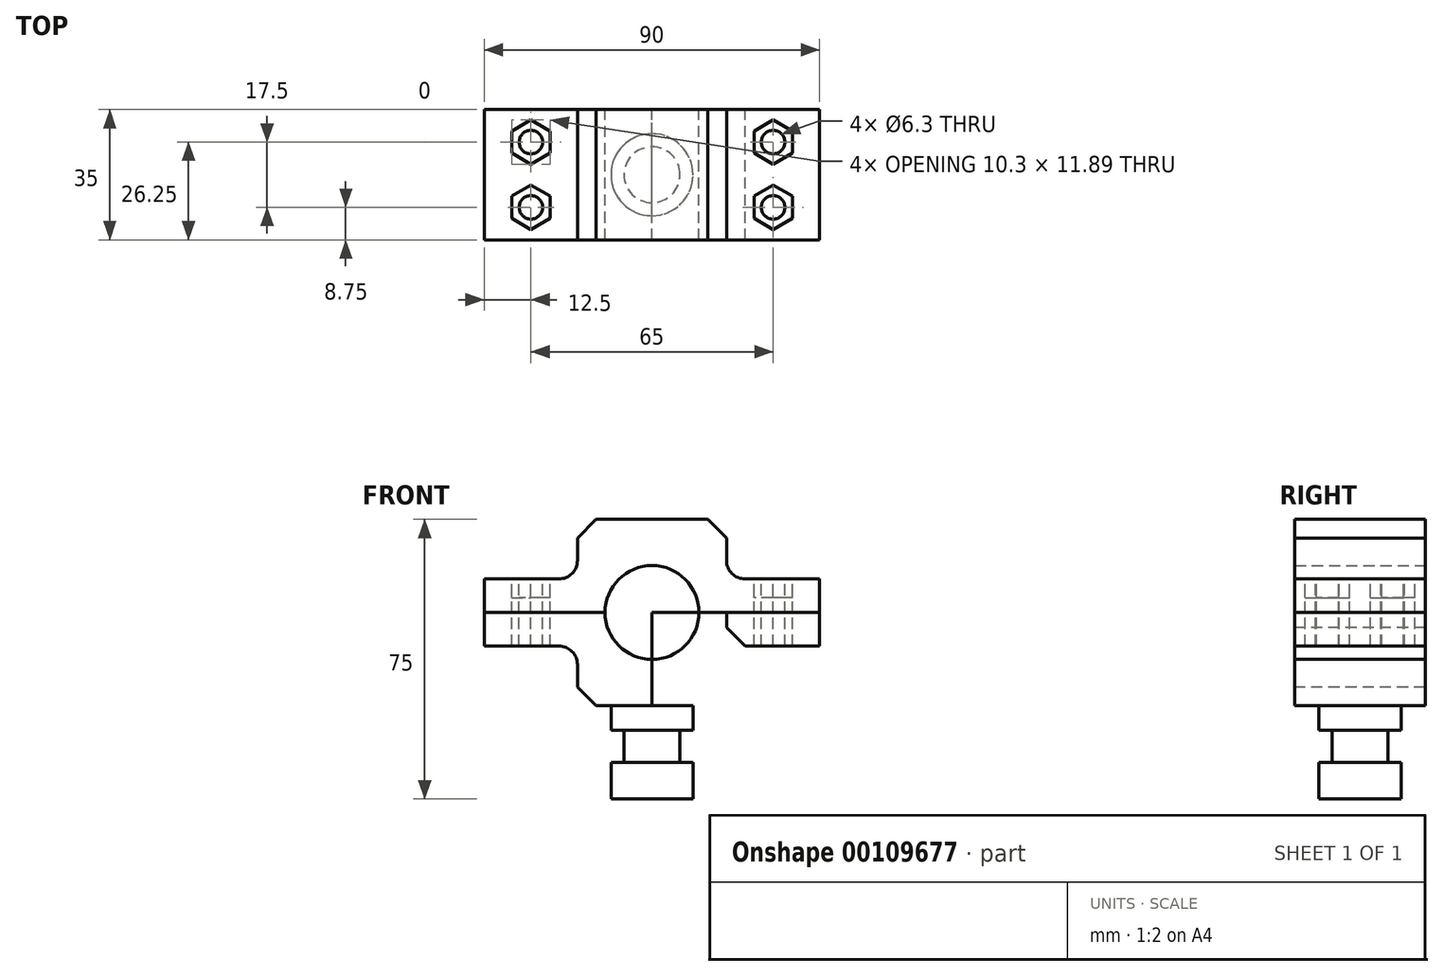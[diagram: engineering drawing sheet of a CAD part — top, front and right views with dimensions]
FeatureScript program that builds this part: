
annotation { "Feature Type Name" : "Feature", "Feature Type Description" : "" }
export const myFeature = defineFeature(function(context is Context, id is Id, definition is map)
    precondition{}
    {
        {
            var Q0;
            Q0=qCreatedBy(makeId("Front.planeOp"),FACE);
            var sketch = newSketch(context, id + "F8", { "sketchPlane" : qUnion([Q0])});
            skArc(sketch, "E0", {"start": v(12.6, 0) * mm, "mid": v(8.9, 8.9) * mm, "end": v(0, 12.6) * mm});
            skLineSegment(sketch, "E1", {"start": v(0, 25) * mm, "end": v(20, 25) * mm});
            skLineSegment(sketch, "E2", {"start": v(20, 25) * mm, "end": v(20, 0) * mm});
            skLineSegment(sketch, "E3", {"start": v(20, 0) * mm, "end": v(45, 0) * mm});
            skLineSegment(sketch, "E4", {"start": v(45, 0) * mm, "end": v(45, 9) * mm});
            skLineSegment(sketch, "E5", {"start": v(45, 9) * mm, "end": v(45, 9) * mm});
            skLineSegment(sketch, "E6", {"start": v(20, 9) * mm, "end": v(45, 9) * mm});
            skLineSegment(sketch, "E7", {"start": v(0, 28.76) * mm, "end": v(0, -27.9) * mm});
            skLineSegment(sketch, "E8", {"start": v(-45, 0) * mm, "end": v(28.7, 0) * mm});
            skLineSegment(sketch, "E9.MirrorCS", {"start": v(0, 25) * mm, "end": v(-20, 25) * mm});
            skArc(sketch, "E10.MirrorCS", {"start": v(-12.6, 0) * mm, "mid": v(-8.9, 8.9) * mm, "end": v(0, 12.6) * mm});
            skLineSegment(sketch, "E11.MirrorCS", {"start": v(-20, 25) * mm, "end": v(-20, 0) * mm});
            skLineSegment(sketch, "E12.MirrorCS", {"start": v(-20, 9) * mm, "end": v(-45, 9) * mm});
            skLineSegment(sketch, "E13.MirrorCS", {"start": v(-45, 0) * mm, "end": v(-45, 9) * mm});
            skArc(sketch, "E14.MirrorCS", {"start": v(12.6, 0) * mm, "mid": v(8.9, -8.9) * mm, "end": v(0, -12.6) * mm});
            skArc(sketch, "E15.MirrorCS", {"start": v(-12.6, 0) * mm, "mid": v(-8.9, -8.9) * mm, "end": v(0, -12.6) * mm});
            skLineSegment(sketch, "E16.MirrorCS", {"start": v(0, -25) * mm, "end": v(20, -25) * mm});
            skLineSegment(sketch, "E17.MirrorCS", {"start": v(20, -25) * mm, "end": v(20, 0) * mm});
            skLineSegment(sketch, "E18.MirrorCS", {"start": v(20, -9) * mm, "end": v(45, -9) * mm});
            skLineSegment(sketch, "E19.MirrorCS", {"start": v(45, 0) * mm, "end": v(45, -9) * mm});
            skLineSegment(sketch, "E20.MirrorCS", {"start": v(0, -25) * mm, "end": v(-20, -25) * mm});
            skLineSegment(sketch, "E21.MirrorCS", {"start": v(-20, -25) * mm, "end": v(-20, 0) * mm});
            skLineSegment(sketch, "E22.MirrorCS", {"start": v(-20, -9) * mm, "end": v(-45, -9) * mm});
            skLineSegment(sketch, "E23.MirrorCS", {"start": v(-45, 0) * mm, "end": v(-45, -9) * mm});
            skSolve(sketch);
        }
        {
            var Q0;
            {var subQ2=sQuery(id+"F8.wireOp",EDGE,"E9.MirrorCS");Q0=makeQuery(id+"F8.imprint","IMPRINT",FACE,{"disambiguationData":[TD([[makeQuery(id+"F8.imprint","IMPRINT",EDGE,{"derivedFrom":subQ2}),1.0]])]});}
            var Q1;
            {var subQ4=sQuery(id+"F8.wireOp",EDGE,"E4");Q1=makeQuery(id+"F8.imprint","IMPRINT",FACE,{"disambiguationData":[TD([[makeQuery(id+"F8.imprint","IMPRINT",EDGE,{"derivedFrom":subQ4}),1.0]])]});}
            var Q2;
            {var subQ4=sQuery(id+"F8.wireOp",EDGE,"E12.MirrorCS");Q2=makeQuery(id+"F8.imprint","IMPRINT",FACE,{"disambiguationData":[TD([[makeQuery(id+"F8.imprint","IMPRINT",EDGE,{"derivedFrom":subQ4}),1.0]])]});}
            var Q3;
            {var subQ5=sQuery(id+"F8.wireOp",EDGE,"E0");Q3=makeQuery(id+"F8.imprint","IMPRINT",FACE,{"disambiguationData":[TD([[makeQuery(id+"F8.imprint","IMPRINT",EDGE,{"derivedFrom":subQ5}),-1.0]])]});}
            extrude(context, id + "F9", {"entities" : qUnion([Q0, Q1, Q2, Q3]), "depth" : 35 * mm});
        }
        {
            var Q0;
            Q0=makeQuery(id+"F9.opExtrude","SWEPT_FACE",FACE,{"disambiguationData":[OSD([sQuery(id+"F8.wireOp",EDGE,"E6")])]});
            var sketch = newSketch(context, id + "F0", { "sketchPlane" : qUnion([Q0])});
            skLineSegment(sketch, "E24", {"start": v(20, -17.5) * mm, "end": v(45, -17.5) * mm, "construction": true});
            skLineSegment(sketch, "E25", {"start": v(20, -8.75) * mm, "end": v(45, -8.75) * mm, "construction": true});
            skLineSegment(sketch, "E26", {"start": v(45, -17.5) * mm, "end": v(45, -8.75) * mm});
            skCircle(sketch, "E27.cCircle", {"center": v(32.5, -8.75) * mm, "radius": 5.95 * mm, "construction": true});
            skPoint(sketch, "E27.cCircle.perimeterSnap0", {"position": v(32.5, -8.75) * mm});
            skLineSegment(sketch, "E27.0", {"start": v(32.5, -14.7) * mm, "end": v(27.35, -11.72) * mm});
            skPoint(sketch, "E27.0.startSnap0", {"position": v(32.5, -8.75) * mm});
            skLineSegment(sketch, "E27.1", {"start": v(27.35, -11.72) * mm, "end": v(27.35, -5.78) * mm});
            skLineSegment(sketch, "E27.2", {"start": v(27.35, -5.78) * mm, "end": v(32.5, -2.8) * mm});
            skLineSegment(sketch, "E27.3", {"start": v(32.5, -2.8) * mm, "end": v(37.65, -5.78) * mm});
            skLineSegment(sketch, "E27.4", {"start": v(37.65, -5.78) * mm, "end": v(37.65, -11.72) * mm});
            skLineSegment(sketch, "E27.5", {"start": v(37.65, -11.72) * mm, "end": v(32.5, -14.7) * mm});
            skLineSegment(sketch, "E28.MirrorCS", {"start": v(32.5, -32.2) * mm, "end": v(37.65, -29.22) * mm});
            skLineSegment(sketch, "E29.MirrorCS", {"start": v(20, -26.25) * mm, "end": v(45, -26.25) * mm, "construction": true});
            skCircle(sketch, "E30.MirrorC", {"center": v(32.5, -26.25) * mm, "radius": 5.95 * mm, "construction": true});
            skLineSegment(sketch, "E31.MirrorCS", {"start": v(37.65, -29.22) * mm, "end": v(37.65, -23.28) * mm});
            skLineSegment(sketch, "E32.MirrorCS", {"start": v(27.35, -29.22) * mm, "end": v(32.5, -32.2) * mm});
            skLineSegment(sketch, "E33.MirrorCS", {"start": v(27.35, -23.28) * mm, "end": v(27.35, -29.22) * mm});
            skLineSegment(sketch, "E34.MirrorCS", {"start": v(37.65, -23.28) * mm, "end": v(32.5, -20.3) * mm});
            skLineSegment(sketch, "E35.MirrorCS", {"start": v(32.5, -20.3) * mm, "end": v(27.35, -23.28) * mm});
            skLineSegment(sketch, "E36.0.0", {"start": v(20, 0) * mm, "end": v(-20, 0) * mm});
            skLineSegment(sketch, "E36.0.1", {"start": v(-20, 0) * mm, "end": v(-20, -35) * mm});
            skLineSegment(sketch, "E36.0.2", {"start": v(-20, -35) * mm, "end": v(20, -35) * mm});
            skLineSegment(sketch, "E36.0.3", {"start": v(20, -35) * mm, "end": v(20, 0) * mm});
            skLineSegment(sketch, "E37", {"start": v(0, 0) * mm, "end": v(0, -35) * mm, "construction": true});
            skCircle(sketch, "E38.MirrorC", {"center": v(-32.5, -8.75) * mm, "radius": 5.95 * mm, "construction": true});
            skLineSegment(sketch, "E39.MirrorCS", {"start": v(-32.5, -2.8) * mm, "end": v(-37.65, -5.78) * mm});
            skLineSegment(sketch, "E40.MirrorCS", {"start": v(-27.35, -5.78) * mm, "end": v(-32.5, -2.8) * mm});
            skLineSegment(sketch, "E41.MirrorCS", {"start": v(-27.35, -11.72) * mm, "end": v(-27.35, -5.78) * mm});
            skLineSegment(sketch, "E42.MirrorCS", {"start": v(-32.5, -14.7) * mm, "end": v(-27.35, -11.72) * mm});
            skLineSegment(sketch, "E43.MirrorCS", {"start": v(-37.65, -11.72) * mm, "end": v(-32.5, -14.7) * mm});
            skLineSegment(sketch, "E44.MirrorCS", {"start": v(-37.65, -5.78) * mm, "end": v(-37.65, -11.72) * mm});
            skLineSegment(sketch, "E45.MirrorCS", {"start": v(-37.65, -23.28) * mm, "end": v(-32.5, -20.3) * mm});
            skLineSegment(sketch, "E46.MirrorCS", {"start": v(-37.65, -29.22) * mm, "end": v(-37.65, -23.28) * mm});
            skLineSegment(sketch, "E47.MirrorCS", {"start": v(-32.5, -32.2) * mm, "end": v(-37.65, -29.22) * mm});
            skLineSegment(sketch, "E48.MirrorCS", {"start": v(-27.35, -29.22) * mm, "end": v(-32.5, -32.2) * mm});
            skLineSegment(sketch, "E49.MirrorCS", {"start": v(-27.35, -23.28) * mm, "end": v(-27.35, -29.22) * mm});
            skCircle(sketch, "E50.MirrorC", {"center": v(-32.5, -26.25) * mm, "radius": 5.95 * mm, "construction": true});
            skLineSegment(sketch, "E51.MirrorCS", {"start": v(-32.5, -20.3) * mm, "end": v(-27.35, -23.28) * mm});
            skCircle(sketch, "E52", {"center": v(32.5, -8.75) * mm, "radius": 3.15 * mm});
            skCircle(sketch, "E53.MirrorC", {"center": v(32.5, -26.25) * mm, "radius": 3.15 * mm});
            skCircle(sketch, "E54.MirrorC", {"center": v(-32.5, -8.75) * mm, "radius": 3.15 * mm});
            skCircle(sketch, "E55.MirrorC", {"center": v(-32.5, -26.25) * mm, "radius": 3.15 * mm});
            skLineSegment(sketch, "E56", {"start": v(27.35, -11.72) * mm, "end": v(37.65, -11.72) * mm, "construction": true});
            skLineSegment(sketch, "E57", {"start": v(45, -17.5) * mm, "end": v(45, 0) * mm});
            skLineSegment(sketch, "E58", {"start": v(32.5, -2.8) * mm, "end": v(32.5, -14.7) * mm, "construction": true});
            skSolve(sketch);
        }
        {
            var Q0;
            Q0=makeQuery(id+"F0.imprint","IMPRINT",FACE,{"disambiguationData":[TD([[makeQuery(id+"F0.imprint","IMPRINT",EDGE,{"derivedFrom":sQuery(id+"F0.wireOp",EDGE,"E27.0")}),-1.0]])]});
            var Q1;
            Q1=makeQuery(id+"F0.imprint","IMPRINT",FACE,{"disambiguationData":[TD([[makeQuery(id+"F0.imprint","IMPRINT",EDGE,{"derivedFrom":sQuery(id+"F0.wireOp",EDGE,"E31.MirrorCS")}),1.0]])]});
            var Q2;
            Q2=makeQuery(id+"F0.imprint","IMPRINT",FACE,{"disambiguationData":[TD([[makeQuery(id+"F0.imprint","IMPRINT",EDGE,{"derivedFrom":sQuery(id+"F0.wireOp",EDGE,"E39.MirrorCS")}),1.0]])]});
            var Q3;
            Q3=makeQuery(id+"F0.imprint","IMPRINT",FACE,{"disambiguationData":[TD([[makeQuery(id+"F0.imprint","IMPRINT",EDGE,{"derivedFrom":sQuery(id+"F0.wireOp",EDGE,"E46.MirrorCS")}),-1.0]])]});
            var Q4;
            Q4=makeQuery(id+"F0.imprint","IMPRINT",FACE,{"disambiguationData":[TD([[makeQuery(id+"F0.imprint","IMPRINT",EDGE,{"derivedFrom":sQuery(id+"F0.wireOp",EDGE,"E52")}),1.0]])]});
            var Q5;
            Q5=makeQuery(id+"F0.imprint","IMPRINT",FACE,{"disambiguationData":[TD([[makeQuery(id+"F0.imprint","IMPRINT",EDGE,{"derivedFrom":sQuery(id+"F0.wireOp",EDGE,"E53.MirrorC")}),-1.0]])]});
            var Q6;
            Q6=makeQuery(id+"F0.imprint","IMPRINT",FACE,{"disambiguationData":[TD([[makeQuery(id+"F0.imprint","IMPRINT",EDGE,{"derivedFrom":sQuery(id+"F0.wireOp",EDGE,"E54.MirrorC")}),-1.0]])]});
            var Q7;
            Q7=makeQuery(id+"F0.imprint","IMPRINT",FACE,{"disambiguationData":[TD([[makeQuery(id+"F0.imprint","IMPRINT",EDGE,{"derivedFrom":sQuery(id+"F0.wireOp",EDGE,"E55.MirrorC")}),1.0]])]});
            var Q8;
            {var subQ0=sQuery(id+"F8.wireOp",EDGE,"E8");var subQ1=makeQuery(id+"F8.imprint","INTERSECT",VERTEX,{"derivedFrom":[sQuery(id+"F8.wireOp",EDGE,"E2"),subQ0,sQuery(id+"F8.wireOp",EDGE,"E17.MirrorCS")]});Q8=makeQuery(id+"F9.opExtrude","SWEPT_FACE",FACE,{"disambiguationData":[OSD([subQ0]),TDD([makeQuery(id+"F8.imprint","IMPRINT",EDGE,{"disambiguationData":[TD([[makeQuery(id+"F8.imprint","INTERSECT",VERTEX,{"derivedFrom":[sQuery(id+"F8.wireOp",EDGE,"E0"),subQ0,sQuery(id+"F8.wireOp",EDGE,"E14.MirrorCS")]}),-1.0]])],"derivedFrom":subQ0}),makeQuery(id+"F8.imprint","IMPRINT",EDGE,{"disambiguationData":[TD([[subQ1,-1.0]])],"derivedFrom":subQ0})])]});}
            extrude(context, id + "F10", {"entities" : qUnion([Q0, Q1, Q2, Q3, Q4, Q5, Q6, Q7]), "operationType" : NewBodyOperationType.REMOVE, "oppositeDirection" : true, "endBoundEntityFace" : qUnion([Q8]), "depth" : 5 * mm});
        }
        {
            var Q0;
            Q0=makeQuery(id+"F9.opExtrude","SWEPT_EDGE",EDGE,{"disambiguationData":[OSD([sQuery(id+"F8.wireOp",EDGE,"E9.MirrorCS"),sQuery(id+"F8.wireOp",EDGE,"E11.MirrorCS")])]});
            var Q1;
            Q1=makeQuery(id+"F9.opExtrude","SWEPT_EDGE",EDGE,{"disambiguationData":[OSD([sQuery(id+"F8.wireOp",EDGE,"E1"),sQuery(id+"F8.wireOp",EDGE,"E2")])]});
            chamfer(context, id + "F1", {"entities" : qUnion([Q0, Q1]), "width" : 5 * mm, "tangentPropagation" : true});
        }
        {
            var Q0;
            {var subQ4=sQuery(id+"F8.wireOp",EDGE,"E22.MirrorCS");Q0=makeQuery(id+"F8.imprint","IMPRINT",FACE,{"disambiguationData":[TD([[makeQuery(id+"F8.imprint","IMPRINT",EDGE,{"derivedFrom":subQ4}),-1.0]])]});}
            var Q1;
            {var subQ4=sQuery(id+"F8.wireOp",EDGE,"E18.MirrorCS");Q1=makeQuery(id+"F8.imprint","IMPRINT",FACE,{"disambiguationData":[TD([[makeQuery(id+"F8.imprint","IMPRINT",EDGE,{"derivedFrom":subQ4}),1.0]])]});}
            var Q2;
            {var subQ1=sQuery(id+"F8.wireOp",EDGE,"E15.MirrorCS");Q2=makeQuery(id+"F8.imprint","IMPRINT",FACE,{"disambiguationData":[TD([[makeQuery(id+"F8.imprint","IMPRINT",EDGE,{"derivedFrom":subQ1}),-1.0]])]});}
            var Q3;
            {var subQ0=sQuery(id+"F8.wireOp",EDGE,"E14.MirrorCS");Q3=makeQuery(id+"F8.imprint","IMPRINT",FACE,{"disambiguationData":[TD([[makeQuery(id+"F8.imprint","IMPRINT",EDGE,{"derivedFrom":subQ0}),1.0]])]});}
            var Q4;
            Q4=makeQuery(id+"F9.opExtrude","CAP_FACE",FACE,{"disambiguationData":[OSD([sQuery(id+"F8.wireOp",EDGE,"E0"),sQuery(id+"F8.wireOp",EDGE,"E1"),sQuery(id+"F8.wireOp",EDGE,"E2"),sQuery(id+"F8.wireOp",EDGE,"E3"),sQuery(id+"F8.wireOp",EDGE,"E4"),sQuery(id+"F8.wireOp",EDGE,"E6"),sQuery(id+"F8.wireOp",EDGE,"E8"),sQuery(id+"F8.wireOp",EDGE,"E9.MirrorCS"),sQuery(id+"F8.wireOp",EDGE,"E10.MirrorCS"),sQuery(id+"F8.wireOp",EDGE,"E12.MirrorCS"),sQuery(id+"F8.wireOp",EDGE,"E13.MirrorCS"),sQuery(id+"F8.wireOp",EDGE,"E11.MirrorCS"),sQuery(id+"F8.wireOp",EDGE,"E21.MirrorCS"),sQuery(id+"F8.wireOp",EDGE,"E22.MirrorCS"),sQuery(id+"F8.wireOp",EDGE,"E23.MirrorCS")])],"isStart":false});
            extrude(context, id + "F2", {"entities" : qUnion([Q0, Q1, Q2, Q3]), "endBound" : BoundingType.UP_TO_SURFACE, "endBoundEntityFace" : qUnion([Q4]), "depth" : 30 * mm});
        }
        {
            var Q0;
            Q0=makeQuery(id+"F2.opExtrude","SWEPT_EDGE",EDGE,{"disambiguationData":[OSD([sQuery(id+"F8.wireOp",EDGE,"E20.MirrorCS"),sQuery(id+"F8.wireOp",EDGE,"E21.MirrorCS")])]});
            var Q1;
            Q1=makeQuery(id+"F2.opExtrude","SWEPT_EDGE",EDGE,{"disambiguationData":[OSD([sQuery(id+"F8.wireOp",EDGE,"E16.MirrorCS"),sQuery(id+"F8.wireOp",EDGE,"E17.MirrorCS")])]});
            chamfer(context, id + "F3", {"entities" : qUnion([Q0, Q1]), "width" : 5 * mm, "tangentPropagation" : true});
        }
        {
            var Q0;
            Q0=makeQuery(id+"F2.opExtrude","SWEPT_FACE",FACE,{"disambiguationData":[OSD([sQuery(id+"F8.wireOp",EDGE,"E16.MirrorCS"),sQuery(id+"F8.wireOp",EDGE,"E20.MirrorCS")])]});
            var sketch = newSketch(context, id + "F11", { "sketchPlane" : qUnion([Q0])});
            skLineSegment(sketch, "E59", {"start": v(0, 0) * mm, "end": v(0, 35) * mm, "construction": true});
            skCircle(sketch, "E60", {"center": v(0, 17.5) * mm, "radius": 11 * mm});
            skCircle(sketch, "E61", {"center": v(0, 17.5) * mm, "radius": 7.5 * mm});
            skSolve(sketch);
        }
        {
            var Q0;
            Q0=makeQuery(id+"F11.imprint","IMPRINT",FACE,{"disambiguationData":[TD([[makeQuery(id+"F11.imprint","IMPRINT",EDGE,{"derivedFrom":sQuery(id+"F11.wireOp",EDGE,"E60")}),1.0]])]});
            var Q1;
            Q1=makeQuery(id+"F11.imprint","IMPRINT",FACE,{"disambiguationData":[TD([[makeQuery(id+"F11.imprint","IMPRINT",EDGE,{"derivedFrom":sQuery(id+"F11.wireOp",EDGE,"E61")}),1.0]])]});
            extrude(context, id + "F4", {"entities" : qUnion([Q0, Q1]), "operationType" : NewBodyOperationType.ADD, "depth" : 25 * mm});
        }
        {
            var Q0;
            Q0=makeQuery(id+"F11.imprint","IMPRINT",FACE,{"disambiguationData":[TD([[makeQuery(id+"F11.imprint","IMPRINT",EDGE,{"derivedFrom":sQuery(id+"F11.wireOp",EDGE,"E60")}),1.0]])]});
            extrude(context, id + "F5", {"entities" : qUnion([Q0]), "operationType" : NewBodyOperationType.REMOVE, "depth" : 15.21 * mm, "hasSecondDirection" : true, "secondDirectionOppositeDirection" : false, "secondDirectionDepth" : 6.66 * mm});
        }
        {
            var Q0;
            Q0=makeQuery(id+"F0.imprint","IMPRINT",FACE,{"disambiguationData":[TD([[makeQuery(id+"F0.imprint","IMPRINT",EDGE,{"derivedFrom":sQuery(id+"F0.wireOp",EDGE,"E55.MirrorC")}),1.0]])]});
            var Q1;
            Q1=makeQuery(id+"F0.imprint","IMPRINT",FACE,{"disambiguationData":[TD([[makeQuery(id+"F0.imprint","IMPRINT",EDGE,{"derivedFrom":sQuery(id+"F0.wireOp",EDGE,"E54.MirrorC")}),-1.0]])]});
            var Q2;
            Q2=makeQuery(id+"F0.imprint","IMPRINT",FACE,{"disambiguationData":[TD([[makeQuery(id+"F0.imprint","IMPRINT",EDGE,{"derivedFrom":sQuery(id+"F0.wireOp",EDGE,"E52")}),1.0]])]});
            var Q3;
            Q3=makeQuery(id+"F0.imprint","IMPRINT",FACE,{"disambiguationData":[TD([[makeQuery(id+"F0.imprint","IMPRINT",EDGE,{"derivedFrom":sQuery(id+"F0.wireOp",EDGE,"E53.MirrorC")}),-1.0]])]});
            var Q4;
            Q4=makeQuery(id+"F2.opExtrude","SWEPT_BODY",BODY,{"disambiguationData":[OSD([sQuery(id+"F8.wireOp",EDGE,"E8"),sQuery(id+"F8.wireOp",EDGE,"E14.MirrorCS"),sQuery(id+"F8.wireOp",EDGE,"E15.MirrorCS"),sQuery(id+"F8.wireOp",EDGE,"E16.MirrorCS"),sQuery(id+"F8.wireOp",EDGE,"E17.MirrorCS"),sQuery(id+"F8.wireOp",EDGE,"E18.MirrorCS"),sQuery(id+"F8.wireOp",EDGE,"E19.MirrorCS"),sQuery(id+"F8.wireOp",EDGE,"E20.MirrorCS"),sQuery(id+"F8.wireOp",EDGE,"E21.MirrorCS"),sQuery(id+"F8.wireOp",EDGE,"E22.MirrorCS"),sQuery(id+"F8.wireOp",EDGE,"E23.MirrorCS")])]});
            extrude(context, id + "F6", {"entities" : qUnion([Q0, Q1, Q2, Q3]), "operationType" : NewBodyOperationType.REMOVE, "endBound" : BoundingType.THROUGH_ALL, "oppositeDirection" : true, "endBoundEntityBody" : qUnion([Q4]), "depth" : 25 * mm});
        }
        {
            var Q0;
            Q0=makeQuery(id+"F9.opExtrude","SWEPT_EDGE",EDGE,{"disambiguationData":[OSD([sQuery(id+"F8.wireOp",EDGE,"E12.MirrorCS"),sQuery(id+"F8.wireOp",EDGE,"E11.MirrorCS")])]});
            var Q1;
            Q1=makeQuery(id+"F9.opExtrude","SWEPT_EDGE",EDGE,{"disambiguationData":[OSD([sQuery(id+"F8.wireOp",EDGE,"E2"),sQuery(id+"F8.wireOp",EDGE,"E6")])]});
            var Q2;
            Q2=makeQuery(id+"F2.opExtrude","SWEPT_EDGE",EDGE,{"disambiguationData":[OSD([sQuery(id+"F8.wireOp",EDGE,"E17.MirrorCS"),sQuery(id+"F8.wireOp",EDGE,"E18.MirrorCS")])]});
            var Q3;
            Q3=makeQuery(id+"F2.opExtrude","SWEPT_EDGE",EDGE,{"disambiguationData":[OSD([sQuery(id+"F8.wireOp",EDGE,"E21.MirrorCS"),sQuery(id+"F8.wireOp",EDGE,"E22.MirrorCS")])]});
            fillet(context, id + "F7", {"entities" : qUnion([Q0, Q1, Q2, Q3]), "radius" : 5 * mm, "tangentPropagation" : true, "allowEdgeOverflow" : false});
        }
    });
